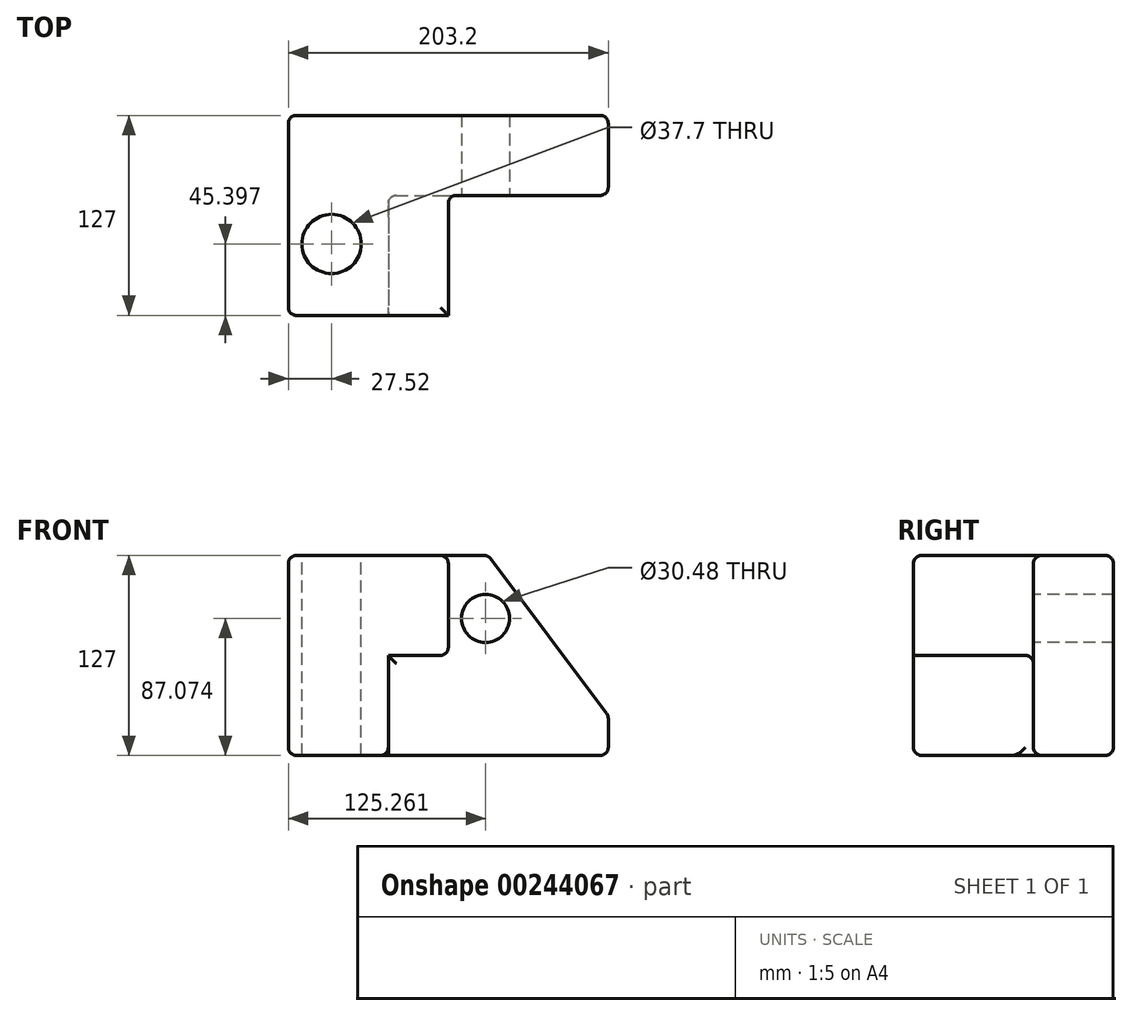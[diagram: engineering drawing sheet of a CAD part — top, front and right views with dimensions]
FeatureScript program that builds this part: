
annotation { "Feature Type Name" : "Feature", "Feature Type Description" : "" }
export const myFeature = defineFeature(function(context is Context, id is Id, definition is map)
    precondition{}
    {
        {
            var Q0;
            Q0=qCreatedBy(makeId("Front.planeOp"),FACE);
            var sketch = newSketch(context, id + "F0", { "sketchPlane" : qUnion([Q0])});
            skLineSegment(sketch, "E0.bottom", {"start": v(-101.6, 63.5) * mm, "end": v(101.6, 63.5) * mm});
            skLineSegment(sketch, "E0.top", {"start": v(-101.6, -63.5) * mm, "end": v(101.6, -63.5) * mm});
            skLineSegment(sketch, "E0.left", {"start": v(-101.6, 63.5) * mm, "end": v(-101.6, -63.5) * mm});
            skLineSegment(sketch, "E0.right", {"start": v(101.6, 63.5) * mm, "end": v(101.6, -63.5) * mm});
            skPoint(sketch, "E0.middle", {"position": v(0, 0) * mm});
            skSolve(sketch);
        }
        {
            var Q0;
            Q0=makeQuery(id+"F0.imprint","IMPRINT",FACE,{"disambiguationData":[TD([[makeQuery(id+"F0.imprint","IMPRINT",EDGE,{"derivedFrom":sQuery(id+"F0.wireOp",EDGE,"E0.bottom")}),-1.0]])]});
            extrude(context, id + "F1", {"entities" : qUnion([Q0]), "depth" : 127 * mm});
        }
        {
            var Q0;
            Q0=makeQuery(id+"F1.opExtrude","CAP_FACE",FACE,{"disambiguationData":[OSD([sQuery(id+"F0.wireOp",EDGE,"E0.bottom"),sQuery(id+"F0.wireOp",EDGE,"E0.top"),sQuery(id+"F0.wireOp",EDGE,"E0.left"),sQuery(id+"F0.wireOp",EDGE,"E0.right")])],"isStart":false});
            var sketch = newSketch(context, id + "F2", { "sketchPlane" : qUnion([Q0])});
            skLineSegment(sketch, "E1", {"start": v(-101.6, -63.5) * mm, "end": v(-38.1, -63.5) * mm});
            skLineSegment(sketch, "E2", {"start": v(-38.1, -63.5) * mm, "end": v(-38.1, 0) * mm});
            skLineSegment(sketch, "E3", {"start": v(-38.1, 0) * mm, "end": v(0, 0) * mm});
            skLineSegment(sketch, "E4", {"start": v(0, 0) * mm, "end": v(0, 63.5) * mm});
            skSolve(sketch);
        }
        {
            var Q0;
            {var subQ2=sQuery(id+"F2.wireOp",EDGE,"E2");Q0=makeQuery(id+"F2.imprint","IMPRINT",FACE,{"disambiguationData":[TD([[makeQuery(id+"F2.imprint","IMPRINT",EDGE,{"derivedFrom":subQ2}),-1.0]])]});}
            extrude(context, id + "F3", {"entities" : qUnion([Q0]), "operationType" : NewBodyOperationType.REMOVE, "oppositeDirection" : true, "depth" : 76.2 * mm});
        }
        {
            var Q0;
            Q0=makeQuery(id+"F1.opExtrude","SWEPT_EDGE",EDGE,{"disambiguationData":[OSD([sQuery(id+"F0.wireOp",EDGE,"E0.bottom"),sQuery(id+"F0.wireOp",EDGE,"E0.right")])]});
            chamfer(context, id + "F4", {"entities" : qUnion([Q0]), "chamferType" : ChamferType.TWO_OFFSETS, "width1" : 76.2 * mm, "oppositeDirection" : false, "width2" : 101.6 * mm, "tangentPropagation" : true});
        }
        {
            var Q0;
            Q0=makeQuery(id+"F1.opExtrude","CAP_EDGE",EDGE,{"disambiguationData":[OSD([sQuery(id+"F0.wireOp",EDGE,"E0.bottom")])],"isStart":false});
            var Q1;
            Q1=makeQuery(id+"F3.boolean.opBoolean","COPY",EDGE,{"derivedFrom":makeQuery(id+"F3.opExtrude","SWEPT_EDGE",EDGE,{"disambiguationData":[OSD([sQuery(id+"F0.wireOp",EDGE,"E0.bottom"),sQuery(id+"F2.wireOp",EDGE,"E4")])]})});
            var Q2;
            Q2=makeQuery(id+"F3.boolean.opBoolean","COPY",EDGE,{"derivedFrom":makeQuery(id+"F3.opExtrude","CAP_EDGE",EDGE,{"disambiguationData":[OSD([sQuery(id+"F2.wireOp",EDGE,"E4")])],"isStart":true})});
            var Q3;
            Q3=makeQuery(id+"F3.boolean.opBoolean","COPY",EDGE,{"derivedFrom":makeQuery(id+"F3.opExtrude","SWEPT_EDGE",EDGE,{"disambiguationData":[OSD([sQuery(id+"F2.wireOp",EDGE,"E3"),sQuery(id+"F2.wireOp",EDGE,"E4")])]})});
            var Q4;
            Q4=makeQuery(id+"F3.boolean.opBoolean","COPY",EDGE,{"derivedFrom":makeQuery(id+"F3.opExtrude","CAP_EDGE",EDGE,{"disambiguationData":[OSD([sQuery(id+"F2.wireOp",EDGE,"E3")])],"isStart":true})});
            var Q5;
            Q5=makeQuery(id+"F3.boolean.opBoolean","COPY",EDGE,{"derivedFrom":makeQuery(id+"F3.opExtrude","CAP_EDGE",EDGE,{"disambiguationData":[OSD([sQuery(id+"F2.wireOp",EDGE,"E2")])],"isStart":true})});
            var Q6;
            Q6=makeQuery(id+"F1.opExtrude","CAP_EDGE",EDGE,{"disambiguationData":[OSD([sQuery(id+"F0.wireOp",EDGE,"E0.left")])],"isStart":false});
            var Q7;
            Q7=makeQuery(id+"F1.opExtrude","CAP_EDGE",EDGE,{"disambiguationData":[OSD([sQuery(id+"F0.wireOp",EDGE,"E0.left")])],"isStart":true});
            var Q8;
            Q8=makeQuery(id+"F1.opExtrude","SWEPT_FACE",FACE,{"disambiguationData":[OSD([sQuery(id+"F0.wireOp",EDGE,"E0.bottom")])]});
            var Q9;
            Q9=makeQuery(id+"F1.opExtrude","CAP_FACE",FACE,{"disambiguationData":[OSD([sQuery(id+"F0.wireOp",EDGE,"E0.bottom"),sQuery(id+"F0.wireOp",EDGE,"E0.top"),sQuery(id+"F0.wireOp",EDGE,"E0.left"),sQuery(id+"F0.wireOp",EDGE,"E0.right")])],"isStart":true});
            var Q10;
            Q10=makeQuery(id+"F3.boolean.opBoolean","COPY",FACE,{"derivedFrom":makeQuery(id+"F3.opExtrude","CAP_FACE",FACE,{"disambiguationData":[OSD([sQuery(id+"F0.wireOp",EDGE,"E0.bottom"),sQuery(id+"F0.wireOp",EDGE,"E0.top"),sQuery(id+"F0.wireOp",EDGE,"E0.right"),sQuery(id+"F2.wireOp",EDGE,"E2"),sQuery(id+"F2.wireOp",EDGE,"E3"),sQuery(id+"F2.wireOp",EDGE,"E4")])],"isStart":false})});
            var Q11;
            Q11=makeQuery(id+"F1.opExtrude","SWEPT_FACE",FACE,{"disambiguationData":[OSD([sQuery(id+"F0.wireOp",EDGE,"E0.right")])]});
            fillet(context, id + "F5", {"entities" : qUnion([Q0, Q1, Q2, Q3, Q4, Q5, Q6, Q7, Q8, Q9, Q10, Q11]), "radius" : 5.08 * mm, "tangentPropagation" : true, "allowEdgeOverflow" : false});
        }
        {
            var Q0;
            Q0=makeQuery(id+"F1.opExtrude","SWEPT_EDGE",EDGE,{"disambiguationData":[OSD([sQuery(id+"F0.wireOp",EDGE,"E0.top"),sQuery(id+"F0.wireOp",EDGE,"E0.left")])]});
            fillet(context, id + "F6", {"entities" : qUnion([Q0]), "radius" : 5.08 * mm, "tangentPropagation" : true, "allowEdgeOverflow" : false});
        }
        {
            var Q0;
            Q0=makeQuery(id+"F3.boolean.opBoolean","COPY",FACE,{"derivedFrom":makeQuery(id+"F3.opExtrude","CAP_FACE",FACE,{"disambiguationData":[OSD([sQuery(id+"F0.wireOp",EDGE,"E0.bottom"),sQuery(id+"F0.wireOp",EDGE,"E0.top"),sQuery(id+"F0.wireOp",EDGE,"E0.right"),sQuery(id+"F2.wireOp",EDGE,"E2"),sQuery(id+"F2.wireOp",EDGE,"E3"),sQuery(id+"F2.wireOp",EDGE,"E4")])],"isStart":false})});
            var sketch = newSketch(context, id + "F7", { "sketchPlane" : qUnion([Q0])});
            skCircle(sketch, "E5", {"center": v(23.66, 23.57) * mm, "radius": 15.24 * mm});
            skSolve(sketch);
        }
        {
            var Q0;
            Q0=makeQuery(id+"F7.imprint","IMPRINT",FACE,{"disambiguationData":[TD([[makeQuery(id+"F7.imprint","IMPRINT",EDGE,{"derivedFrom":sQuery(id+"F7.wireOp",EDGE,"E5")}),1.0]])]});
            extrude(context, id + "F8", {"entities" : qUnion([Q0]), "operationType" : NewBodyOperationType.REMOVE, "oppositeDirection" : true, "depth" : 50.8 * mm});
        }
        {
            var Q0;
            Q0=makeQuery(id+"F1.opExtrude","SWEPT_FACE",FACE,{"disambiguationData":[OSD([sQuery(id+"F0.wireOp",EDGE,"E0.bottom")])]});
            var sketch = newSketch(context, id + "F9", { "sketchPlane" : qUnion([Q0])});
            skCircle(sketch, "E6", {"center": v(-74.08, -81.6) * mm, "radius": 18.85 * mm});
            skSolve(sketch);
        }
        {
            var Q0;
            Q0=makeQuery(id+"F9.imprint","IMPRINT",FACE,{"disambiguationData":[TD([[makeQuery(id+"F9.imprint","IMPRINT",EDGE,{"derivedFrom":sQuery(id+"F9.wireOp",EDGE,"E6")}),1.0]])]});
            var Q1;
            Q1=makeQuery(id+"F1.opExtrude","SWEPT_FACE",FACE,{"disambiguationData":[OSD([sQuery(id+"F0.wireOp",EDGE,"E0.top")])]});
            extrude(context, id + "F10", {"entities" : qUnion([Q0]), "operationType" : NewBodyOperationType.REMOVE, "endBound" : BoundingType.UP_TO_SURFACE, "oppositeDirection" : true, "endBoundEntityFace" : qUnion([Q1]), "depth" : 25.4 * mm});
        }
    });
